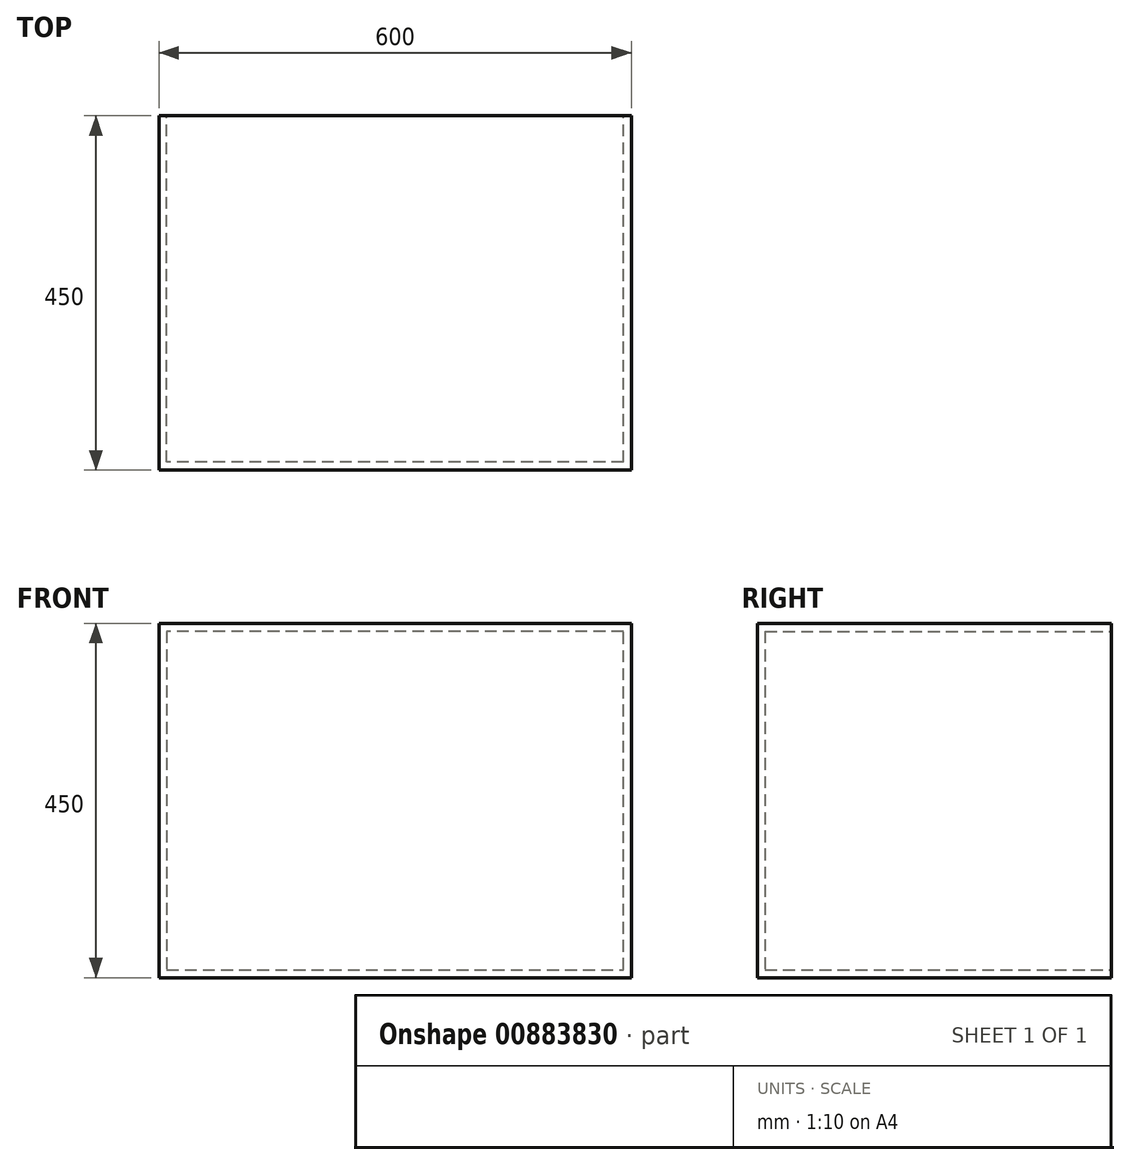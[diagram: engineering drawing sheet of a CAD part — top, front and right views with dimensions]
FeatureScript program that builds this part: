
annotation { "Feature Type Name" : "Feature", "Feature Type Description" : "" }
export const myFeature = defineFeature(function(context is Context, id is Id, definition is map)
    precondition{}
    {
        {
            var Q0;
            Q0=qCreatedBy(makeId("Front.planeOp"),FACE);
            var sketch = newSketch(context, id + "F0", { "sketchPlane" : qUnion([Q0])});
            skLineSegment(sketch, "E0.bottom", {"start": v(-300, 10) * mm, "end": v(300, 10) * mm});
            skLineSegment(sketch, "E0.top", {"start": v(-300, -440) * mm, "end": v(300, -440) * mm});
            skLineSegment(sketch, "E0.left", {"start": v(-300, 10) * mm, "end": v(-300, -440) * mm});
            skLineSegment(sketch, "E0.right", {"start": v(300, 10) * mm, "end": v(300, -440) * mm});
            skLineSegment(sketch, "E1", {"start": v(0, 10) * mm, "end": v(0, 0) * mm});
            skSolve(sketch);
        }
        {
            var Q0;
            Q0=qCreatedBy(makeId("Front.planeOp"),FACE);
            var sketch = newSketch(context, id + "F1", { "sketchPlane" : qUnion([Q0])});
            skLineSegment(sketch, "E2", {"start": v(-290, 0) * mm, "end": v(-290, -430) * mm});
            skLineSegment(sketch, "E3", {"start": v(-290, -430) * mm, "end": v(290, -430) * mm});
            skLineSegment(sketch, "E4", {"start": v(290, -430) * mm, "end": v(290, 0) * mm});
            skLineSegment(sketch, "E5", {"start": v(290, 0) * mm, "end": v(-290, 0) * mm});
            skSolve(sketch);
        }
        {
            var Q0;
            Q0=makeQuery(id+"F0.imprint","IMPRINT",FACE,{"disambiguationData":[TD([[makeQuery(id+"F0.imprint","IMPRINT",EDGE,{"derivedFrom":sQuery(id+"F0.wireOp",EDGE,"E0.bottom")}),-1.0]])]});
            extrude(context, id + "F2", {"entities" : qUnion([Q0]), "depth" : 450 * mm, "offsetDistance" : 25 * mm});
        }
        {
            var Q0;
            Q0 = qSketchRegion(id + "F1", true);
            extrude(context, id + "F3", {"entities" : qUnion([Q0]), "operationType" : NewBodyOperationType.REMOVE, "depth" : 440 * mm, "offsetDistance" : 25 * mm});
        }
    });
